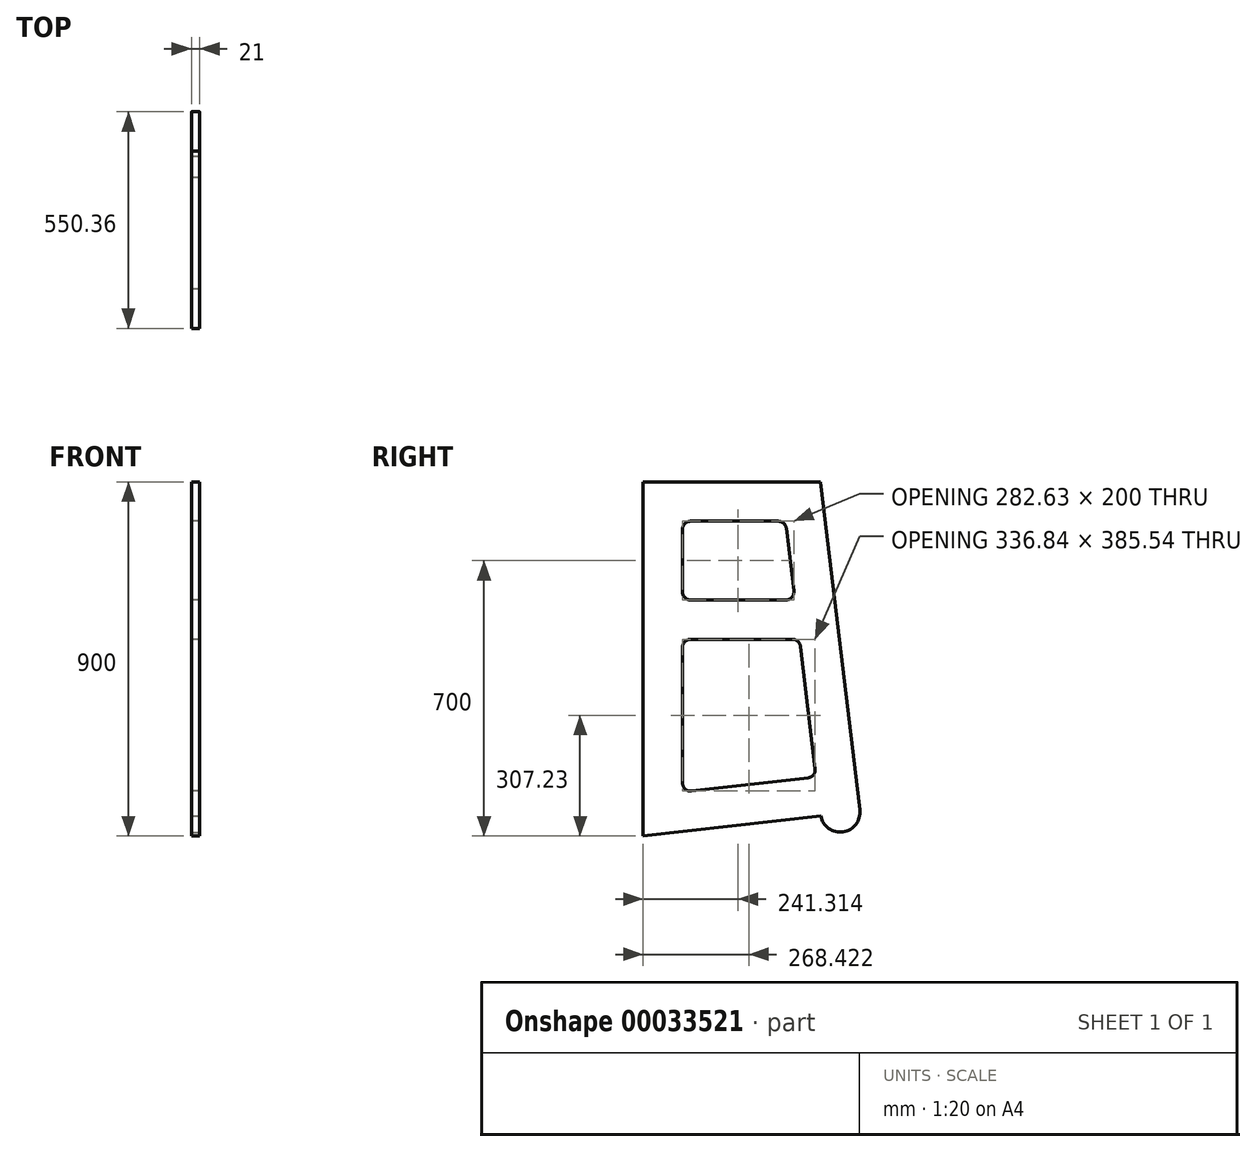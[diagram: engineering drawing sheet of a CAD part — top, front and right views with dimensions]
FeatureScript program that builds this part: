
annotation { "Feature Type Name" : "Feature", "Feature Type Description" : "" }
export const myFeature = defineFeature(function(context is Context, id is Id, definition is map)
    precondition{}
    {
        {
            var Q0;
            Q0=qCreatedBy(makeId("Right.planeOp"),FACE);
            var sketch = newSketch(context, id + "F0", { "sketchPlane" : qUnion([Q0])});
            skLineSegment(sketch, "E0.bottom", {"start": v(1200, 940) * mm, "end": v(0, 940) * mm, "construction": true});
            skLineSegment(sketch, "E0.top", {"start": v(1200, 0) * mm, "end": v(0, 0) * mm, "construction": true});
            skLineSegment(sketch, "E0.left", {"start": v(1200, 940) * mm, "end": v(1200, 0) * mm, "construction": true});
            skLineSegment(sketch, "E0.right", {"start": v(0, 940) * mm, "end": v(0, 0) * mm, "construction": true});
            skLineSegment(sketch, "E1", {"start": v(0, 0) * mm, "end": v(0, 900) * mm});
            skLineSegment(sketch, "E2", {"start": v(0, 900) * mm, "end": v(450, 900) * mm});
            skLineSegment(sketch, "E3", {"start": v(550, 0) * mm, "end": v(0, 0) * mm, "construction": true});
            skLineSegment(sketch, "E4", {"start": v(0, 0) * mm, "end": v(451.15, 51.12) * mm});
            skLineSegment(sketch, "E5", {"start": v(450, 900) * mm, "end": v(550, 65.95) * mm});
            skArc(sketch, "E6", {"start": v(451.15, 51.12) * mm, "mid": v(507.77, 10.55) * mm, "end": v(550, 65.95) * mm});
            skSolve(sketch);
        }
        {
            var Q0;
            Q0=makeQuery(id+"F0.imprint","IMPRINT",FACE,{"disambiguationData":[TD([[makeQuery(id+"F0.imprint","IMPRINT",EDGE,{"derivedFrom":sQuery(id+"F0.wireOp",EDGE,"E1")}),-1.0]])]});
            extrude(context, id + "F1", {"entities" : qUnion([Q0]), "oppositeDirection" : true, "depth" : 21 * mm});
        }
        {
            var Q0;
            Q0=makeQuery(id+"F1.opExtrude","CAP_FACE",FACE,{"disambiguationData":[OSD([sQuery(id+"F0.wireOp",EDGE,"E1"),sQuery(id+"F0.wireOp",EDGE,"E2"),sQuery(id+"F0.wireOp",EDGE,"E4"),sQuery(id+"F0.wireOp",EDGE,"E5"),sQuery(id+"F0.wireOp",EDGE,"E6")])],"isStart":false});
            var sketch = newSketch(context, id + "F2", { "sketchPlane" : qUnion([Q0])});
            skLineSegment(sketch, "E7", {"start": v(-120, 800) * mm, "end": v(-343.53, 800) * mm});
            skLineSegment(sketch, "E8", {"start": v(-363.39, 782.38) * mm, "end": v(-382.57, 622.38) * mm});
            skLineSegment(sketch, "E9", {"start": v(-362.71, 600) * mm, "end": v(-120, 600) * mm});
            skLineSegment(sketch, "E10", {"start": v(-100, 620) * mm, "end": v(-100, 780) * mm});
            skLineSegment(sketch, "E11", {"start": v(-100, 480) * mm, "end": v(-100, 134.37) * mm});
            skLineSegment(sketch, "E12", {"start": v(-120, 500) * mm, "end": v(-379.5, 500) * mm});
            skLineSegment(sketch, "E13", {"start": v(-399.36, 482.38) * mm, "end": v(-436.76, 170.39) * mm});
            skLineSegment(sketch, "E14", {"start": v(-419.16, 148.13) * mm, "end": v(-122.25, 114.5) * mm});
            skPoint(sketch, "E15.visualSharp", {"position": v(-100, 800) * mm});
            skArc(sketch, "E15.filletArc", {"start": v(-100, 780) * mm, "mid": v(-105.86, 794.14) * mm, "end": v(-120, 800) * mm});
            skPoint(sketch, "E16.visualSharp", {"position": v(-100, 600) * mm});
            skArc(sketch, "E16.filletArc", {"start": v(-120, 600) * mm, "mid": v(-105.86, 605.86) * mm, "end": v(-100, 620) * mm});
            skPoint(sketch, "E17.visualSharp", {"position": v(-100, 500) * mm});
            skArc(sketch, "E17.filletArc", {"start": v(-100, 480) * mm, "mid": v(-105.86, 494.14) * mm, "end": v(-120, 500) * mm});
            skPoint(sketch, "E18.visualSharp", {"position": v(-100, 111.97) * mm});
            skArc(sketch, "E18.filletArc", {"start": v(-122.25, 114.5) * mm, "mid": v(-106.68, 119.45) * mm, "end": v(-100, 134.37) * mm});
            skPoint(sketch, "E19.visualSharp", {"position": v(-397.24, 500) * mm});
            skArc(sketch, "E19.filletArc", {"start": v(-379.5, 500) * mm, "mid": v(-392.77, 494.96) * mm, "end": v(-399.36, 482.38) * mm});
            skPoint(sketch, "E20.visualSharp", {"position": v(-361.27, 800) * mm});
            skArc(sketch, "E20.filletArc", {"start": v(-343.53, 800) * mm, "mid": v(-356.8, 794.96) * mm, "end": v(-363.39, 782.38) * mm});
            skPoint(sketch, "E21.visualSharp", {"position": v(-385.25, 600) * mm});
            skArc(sketch, "E21.filletArc", {"start": v(-382.57, 622.38) * mm, "mid": v(-377.67, 606.73) * mm, "end": v(-362.71, 600) * mm});
            skPoint(sketch, "E22.visualSharp", {"position": v(-439.16, 150.4) * mm});
            skArc(sketch, "E22.filletArc", {"start": v(-436.76, 170.39) * mm, "mid": v(-432.59, 155.6) * mm, "end": v(-419.16, 148.13) * mm});
            skCircle(sketch, "E23", {"center": v(-500.36, 60) * mm, "radius": 4 * mm});
            skSolve(sketch);
        }
        {
            var Q0;
            Q0=makeQuery(id+"F2.imprint","IMPRINT",FACE,{"disambiguationData":[TD([[makeQuery(id+"F2.imprint","IMPRINT",EDGE,{"derivedFrom":sQuery(id+"F2.wireOp",EDGE,"E7")}),1.0]])]});
            var Q1;
            Q1=makeQuery(id+"F2.imprint","IMPRINT",FACE,{"disambiguationData":[TD([[makeQuery(id+"F2.imprint","IMPRINT",EDGE,{"derivedFrom":sQuery(id+"F2.wireOp",EDGE,"E11")}),-1.0]])]});
            extrude(context, id + "F3", {"entities" : qUnion([Q0, Q1]), "operationType" : NewBodyOperationType.REMOVE, "oppositeDirection" : true, "depth" : 25 * mm});
        }
    });
